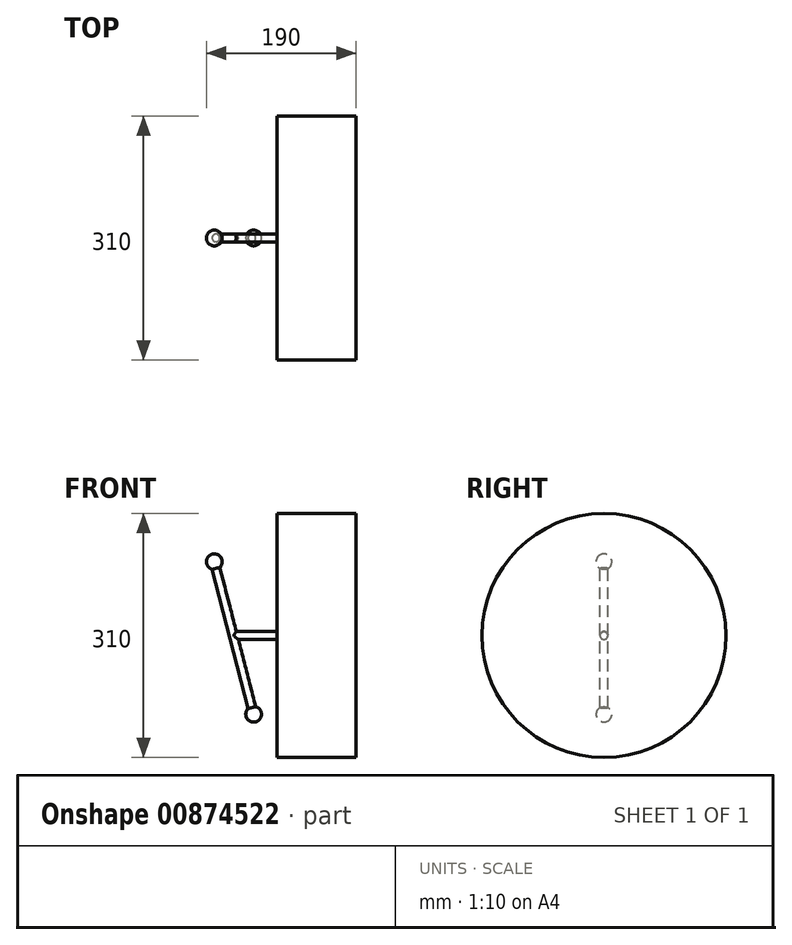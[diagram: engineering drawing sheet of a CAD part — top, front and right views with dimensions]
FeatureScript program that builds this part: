
annotation { "Feature Type Name" : "Feature", "Feature Type Description" : "" }
export const myFeature = defineFeature(function(context is Context, id is Id, definition is map)
    precondition{}
    {
        {
            var Q0;
            Q0=qCreatedBy(makeId("Front.planeOp"),FACE);
            var sketch = newSketch(context, id + "F0", { "sketchPlane" : qUnion([Q0])});
            skArc(sketch, "E0", {"start": v(-43, 86.51) * mm, "mid": v(-41.3, 98.57) * mm, "end": v(-52.5, 103.33) * mm});
            skArc(sketch, "E1", {"start": v(2.5, -109.68) * mm, "mid": v(10, -100.1) * mm, "end": v(2.68, -90.36) * mm});
            skLineSegment(sketch, "E2", {"start": v(-52.5, 103.33) * mm, "end": v(2.5, -109.68) * mm});
            skLineSegment(sketch, "E3", {"start": v(-43, 86.51) * mm, "end": v(2.68, -90.36) * mm});
            skSolve(sketch);
        }
        {
            var Q0;
            Q0=makeQuery(id+"F0.imprint","IMPRINT",FACE,{"disambiguationData":[TD([[makeQuery(id+"F0.imprint","IMPRINT",EDGE,{"derivedFrom":sQuery(id+"F0.wireOp",EDGE,"E0")}),1.0]])]});
            var Q1;
            Q1=sQuery(id+"F0.wireOp",EDGE,"E2");
            revolve(context, id + "F1", {"surfaceOperationType" : NewSurfaceOperationType.NEW, "entities" : qUnion([Q0]), "axis" : qUnion([Q1]), "revolveType" : RevolveType.FULL});
        }
        {
            var Q0;
            Q0=qCreatedBy(makeId("Front.planeOp"),FACE);
            var sketch = newSketch(context, id + "F2", { "sketchPlane" : qUnion([Q0])});
            skLineSegment(sketch, "E4", {"start": v(-25, 5) * mm, "end": v(30, 5) * mm});
            skLineSegment(sketch, "E5", {"start": v(30, 5) * mm, "end": v(30, 155) * mm});
            skLineSegment(sketch, "E6", {"start": v(30, 155) * mm, "end": v(130, 155) * mm});
            skLineSegment(sketch, "E7", {"start": v(130, 155) * mm, "end": v(130, 0) * mm});
            skLineSegment(sketch, "E8", {"start": v(130, 0) * mm, "end": v(-25, 0) * mm});
            skLineSegment(sketch, "E9", {"start": v(-25, 0) * mm, "end": v(-25, 5) * mm});
            skSolve(sketch);
        }
        {
            var Q0;
            Q0=makeQuery(id+"F2.imprint","IMPRINT",FACE,{"disambiguationData":[TD([[makeQuery(id+"F2.imprint","IMPRINT",EDGE,{"derivedFrom":sQuery(id+"F2.wireOp",EDGE,"E4")}),-1.0]])]});
            var Q1;
            Q1=sQuery(id+"F2.wireOp",EDGE,"E8");
            revolve(context, id + "F3", {"operationType" : NewBodyOperationType.ADD, "surfaceOperationType" : NewSurfaceOperationType.NEW, "entities" : qUnion([Q0]), "axis" : qUnion([Q1]), "revolveType" : RevolveType.FULL});
        }
    });
